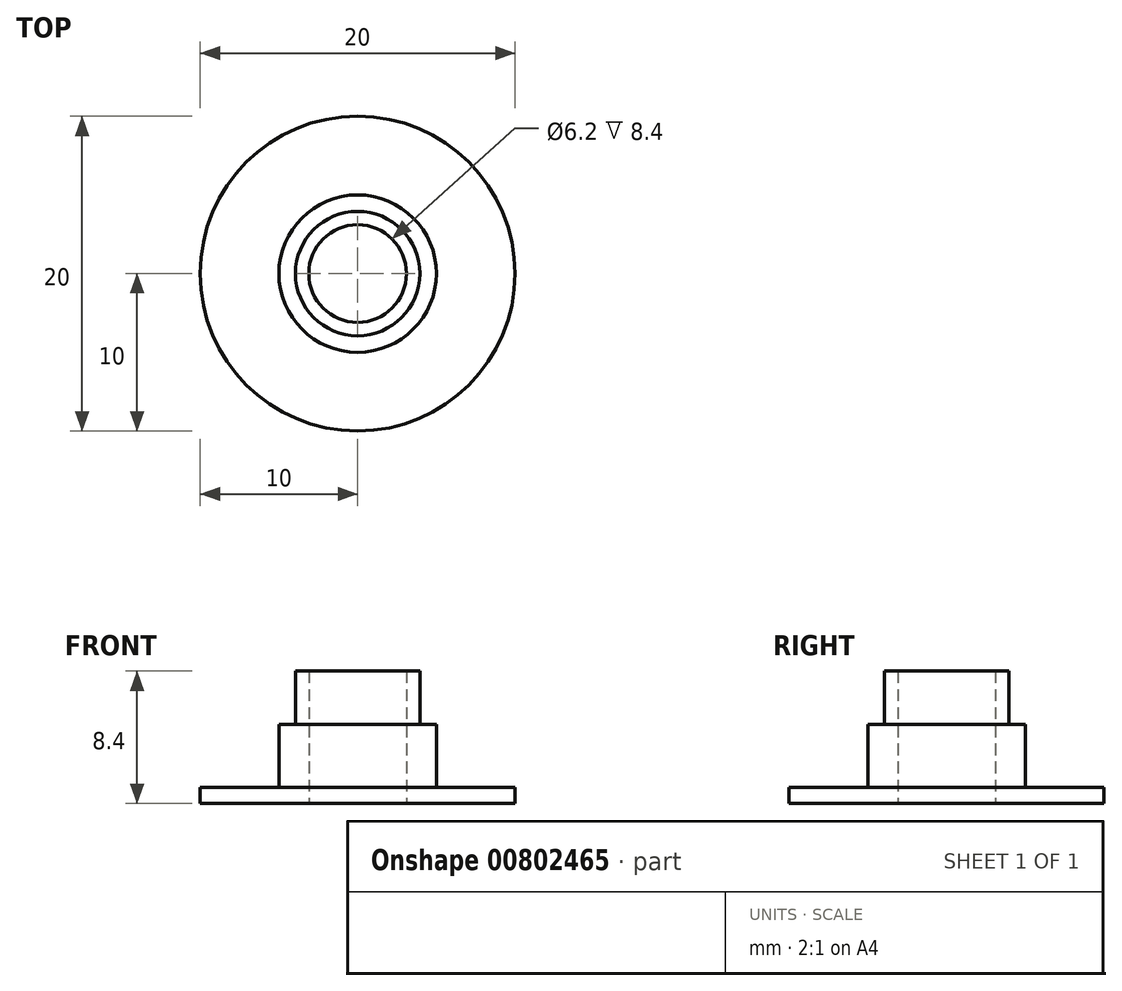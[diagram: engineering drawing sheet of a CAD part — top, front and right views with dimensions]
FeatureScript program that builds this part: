
annotation { "Feature Type Name" : "Feature", "Feature Type Description" : "" }
export const myFeature = defineFeature(function(context is Context, id is Id, definition is map)
    precondition{}
    {
        {
            var Q0;
            Q0=qCreatedBy(makeId("Top.planeOp"),FACE);
            var sketch = newSketch(context, id + "F0", { "sketchPlane" : qUnion([Q0])});
            skPoint(sketch, "E0.middle", {"position": v(0, 0) * mm});
            skCircle(sketch, "E1", {"center": v(0, 0) * mm, "radius": 3.95 * mm});
            skCircle(sketch, "E2", {"center": v(0, 0) * mm, "radius": 3.1 * mm});
            skCircle(sketch, "E3", {"center": v(0, 0) * mm, "radius": 5 * mm});
            skCircle(sketch, "E4", {"center": v(0, 0) * mm, "radius": 10 * mm});
            skSolve(sketch);
        }
        {
            var Q0;
            Q0=makeQuery(id+"F0.imprint","IMPRINT",FACE,{"disambiguationData":[TD([[makeQuery(id+"F0.imprint","IMPRINT",EDGE,{"derivedFrom":sQuery(id+"F0.wireOp",EDGE,"E1")}),1.0]])]});
            extrude(context, id + "F1", {"entities" : qUnion([Q0]), "depth" : 8.4 * mm, "offsetDistance" : 25 * mm});
        }
        {
            var Q0;
            Q0=makeQuery(id+"F0.imprint","IMPRINT",FACE,{"disambiguationData":[TD([[makeQuery(id+"F0.imprint","IMPRINT",EDGE,{"derivedFrom":sQuery(id+"F0.wireOp",EDGE,"E1")}),-1.0]])]});
            extrude(context, id + "F2", {"entities" : qUnion([Q0]), "operationType" : NewBodyOperationType.ADD, "depth" : 5 * mm, "offsetDistance" : 25 * mm});
        }
        {
            var Q0;
            Q0=makeQuery(id+"F0.imprint","IMPRINT",FACE,{"disambiguationData":[TD([[makeQuery(id+"F0.imprint","IMPRINT",EDGE,{"derivedFrom":sQuery(id+"F0.wireOp",EDGE,"E3")}),-1.0]])]});
            extrude(context, id + "F3", {"entities" : qUnion([Q0]), "operationType" : NewBodyOperationType.ADD, "depth" : 1 * mm, "offsetDistance" : 25 * mm});
        }
    });
